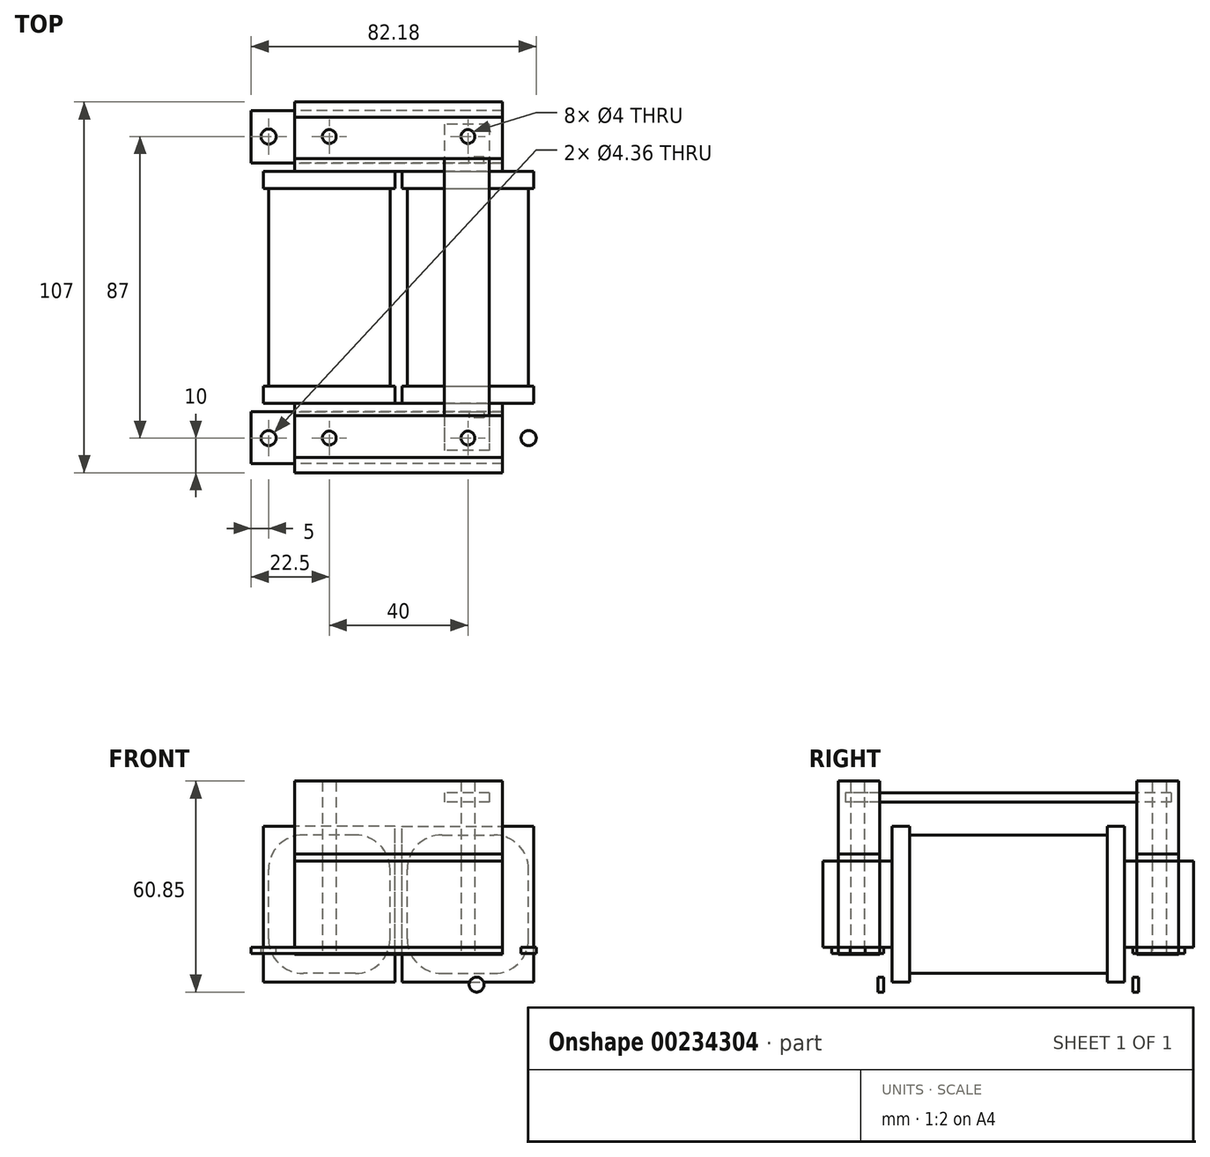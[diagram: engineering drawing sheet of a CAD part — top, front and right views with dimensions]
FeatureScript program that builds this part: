
annotation { "Feature Type Name" : "Feature", "Feature Type Description" : "" }
export const myFeature = defineFeature(function(context is Context, id is Id, definition is map)
    precondition{}
    {
        {
            var Q0;
            Q0=qCreatedBy(makeId("Front.planeOp"),FACE);
            var sketch = newSketch(context, id + "F0", { "sketchPlane" : qUnion([Q0])});
            skLineSegment(sketch, "E0.bottom", {"start": v(30, -12.5) * mm, "end": v(-30, -12.5) * mm});
            skLineSegment(sketch, "E0.top", {"start": v(30, 12.5) * mm, "end": v(-30, 12.5) * mm});
            skLineSegment(sketch, "E0.left", {"start": v(30, -12.5) * mm, "end": v(30, 12.5) * mm});
            skLineSegment(sketch, "E0.right", {"start": v(-30, -12.5) * mm, "end": v(-30, 12.5) * mm});
            skPoint(sketch, "E0.middle", {"position": v(0, 0) * mm});
            skLineSegment(sketch, "E1", {"start": v(-10, -12.5) * mm, "end": v(-10, 12.5) * mm});
            skLineSegment(sketch, "E2.MirrorCS", {"start": v(10, -12.5) * mm, "end": v(10, 12.5) * mm});
            skPoint(sketch, "E3", {"position": v(-20, 0) * mm});
            skLineSegment(sketch, "E4.bottom", {"start": v(-1, -22.5) * mm, "end": v(-39, -22.5) * mm});
            skLineSegment(sketch, "E4.top", {"start": v(-1, 22.5) * mm, "end": v(-39, 22.5) * mm});
            skLineSegment(sketch, "E4.left", {"start": v(-1, -22.5) * mm, "end": v(-1, 22.5) * mm});
            skLineSegment(sketch, "E4.right", {"start": v(-39, -22.5) * mm, "end": v(-39, 22.5) * mm});
            skLineSegment(sketch, "E5.bottom", {"start": v(-12.5, -20) * mm, "end": v(-27.5, -20) * mm});
            skLineSegment(sketch, "E5.top", {"start": v(-12.5, 20) * mm, "end": v(-27.5, 20) * mm});
            skLineSegment(sketch, "E5.left", {"start": v(-2.5, -10) * mm, "end": v(-2.5, 10) * mm});
            skLineSegment(sketch, "E5.right", {"start": v(-37.5, -10) * mm, "end": v(-37.5, 10) * mm});
            skPoint(sketch, "E6.visualSharp", {"position": v(-37.5, 20) * mm});
            skArc(sketch, "E6.filletArc", {"start": v(-27.5, 20) * mm, "mid": v(-34.57, 17.07) * mm, "end": v(-37.5, 10) * mm});
            skPoint(sketch, "E7.visualSharp", {"position": v(-2.5, 20) * mm});
            skArc(sketch, "E7.filletArc", {"start": v(-2.5, 10) * mm, "mid": v(-5.43, 17.07) * mm, "end": v(-12.5, 20) * mm});
            skPoint(sketch, "E8.visualSharp", {"position": v(-2.5, -20) * mm});
            skArc(sketch, "E8.filletArc", {"start": v(-12.5, -20) * mm, "mid": v(-5.43, -17.07) * mm, "end": v(-2.5, -10) * mm});
            skPoint(sketch, "E9.visualSharp", {"position": v(-37.5, -20) * mm});
            skArc(sketch, "E9.filletArc", {"start": v(-37.5, -10) * mm, "mid": v(-34.57, -17.07) * mm, "end": v(-27.5, -20) * mm});
            skLineSegment(sketch, "E10.MirrorCS", {"start": v(1, -22.5) * mm, "end": v(1, 22.5) * mm});
            skLineSegment(sketch, "E11.MirrorCS", {"start": v(1, 22.5) * mm, "end": v(39, 22.5) * mm});
            skLineSegment(sketch, "E12.MirrorCS", {"start": v(39, -22.5) * mm, "end": v(39, 22.5) * mm});
            skLineSegment(sketch, "E13.MirrorCS", {"start": v(1, -22.5) * mm, "end": v(39, -22.5) * mm});
            skLineSegment(sketch, "E14.MirrorCS", {"start": v(12.5, 20) * mm, "end": v(27.5, 20) * mm});
            skArc(sketch, "E15.MirrorCS", {"start": v(2.5, 10) * mm, "mid": v(5.43, 17.07) * mm, "end": v(12.5, 20) * mm});
            skLineSegment(sketch, "E16.MirrorCS", {"start": v(2.5, -10) * mm, "end": v(2.5, 10) * mm});
            skArc(sketch, "E17.MirrorCS", {"start": v(12.5, -20) * mm, "mid": v(5.43, -17.07) * mm, "end": v(2.5, -10) * mm});
            skLineSegment(sketch, "E18.MirrorCS", {"start": v(12.5, -20) * mm, "end": v(27.5, -20) * mm});
            skArc(sketch, "E19.MirrorCS", {"start": v(37.5, -10) * mm, "mid": v(34.57, -17.07) * mm, "end": v(27.5, -20) * mm});
            skLineSegment(sketch, "E20.MirrorCS", {"start": v(37.5, -10) * mm, "end": v(37.5, 10) * mm});
            skArc(sketch, "E21.MirrorCS", {"start": v(27.5, 20) * mm, "mid": v(34.57, 17.07) * mm, "end": v(37.5, 10) * mm});
            skSolve(sketch);
        }
        {
            var Q0;
            {var subQ0=sQuery(id+"F0.wireOp",EDGE,"E0.right");Q0=makeQuery(id+"F0.imprint","IMPRINT",FACE,{"disambiguationData":[TD([[makeQuery(id+"F0.imprint","IMPRINT",EDGE,{"derivedFrom":subQ0}),-1.0]])]});}
            var Q1;
            {var subQ0=sQuery(id+"F0.wireOp",EDGE,"E0.left");Q1=makeQuery(id+"F0.imprint","IMPRINT",FACE,{"disambiguationData":[TD([[makeQuery(id+"F0.imprint","IMPRINT",EDGE,{"derivedFrom":subQ0}),1.0]])]});}
            var Q2;
            {var subQ4=sQuery(id+"F0.wireOp",EDGE,"E0.right");Q2=makeQuery(id+"F0.imprint","IMPRINT",FACE,{"disambiguationData":[TD([[makeQuery(id+"F0.imprint","IMPRINT",EDGE,{"derivedFrom":subQ4}),1.0]])]});}
            var Q3;
            {var subQ1=sQuery(id+"F0.wireOp",EDGE,"E1");Q3=makeQuery(id+"F0.imprint","IMPRINT",FACE,{"disambiguationData":[TD([[makeQuery(id+"F0.imprint","IMPRINT",EDGE,{"derivedFrom":subQ1}),-1.0]])]});}
            var Q4;
            {var subQ0=sQuery(id+"F0.wireOp",EDGE,"E2.MirrorCS");Q4=makeQuery(id+"F0.imprint","IMPRINT",FACE,{"disambiguationData":[TD([[makeQuery(id+"F0.imprint","IMPRINT",EDGE,{"derivedFrom":subQ0}),1.0]])]});}
            var Q5;
            {var subQ1=sQuery(id+"F0.wireOp",EDGE,"E0.left");Q5=makeQuery(id+"F0.imprint","IMPRINT",FACE,{"disambiguationData":[TD([[makeQuery(id+"F0.imprint","IMPRINT",EDGE,{"derivedFrom":subQ1}),-1.0]])]});}
            extrude(context, id + "F1", {"entities" : qUnion([Q0, Q1, Q2, Q3, Q4, Q5]), "depth" : 57 * mm, "symmetric" : true});
        }
        {
            var Q0;
            Q0=makeQuery(id+"F1.opExtrude","CAP_FACE",FACE,{"disambiguationData":[OSD([sQuery(id+"F0.wireOp",EDGE,"E5.bottom"),sQuery(id+"F0.wireOp",EDGE,"E5.top"),sQuery(id+"F0.wireOp",EDGE,"E5.left"),sQuery(id+"F0.wireOp",EDGE,"E5.right"),sQuery(id+"F0.wireOp",EDGE,"E6.filletArc"),sQuery(id+"F0.wireOp",EDGE,"E7.filletArc"),sQuery(id+"F0.wireOp",EDGE,"E8.filletArc"),sQuery(id+"F0.wireOp",EDGE,"E9.filletArc")])],"isStart":false});
            var sketch = newSketch(context, id + "F2", { "sketchPlane" : qUnion([Q0])});
            skLineSegment(sketch, "E22.bottom", {"start": v(-1, -22.5) * mm, "end": v(-39, -22.5) * mm});
            skLineSegment(sketch, "E22.top", {"start": v(-1, 22.5) * mm, "end": v(-39, 22.5) * mm});
            skLineSegment(sketch, "E22.left", {"start": v(-1, -22.5) * mm, "end": v(-1, 22.5) * mm});
            skLineSegment(sketch, "E22.right", {"start": v(-39, -22.5) * mm, "end": v(-39, 22.5) * mm});
            skPoint(sketch, "E22.middle", {"position": v(-20, 0) * mm});
            skPoint(sketch, "E22.middle.positionSnap0", {"position": v(-20, 20) * mm});
            skPoint(sketch, "E22.centerSnap0", {"position": v(-20, 20) * mm});
            skSolve(sketch);
        }
        {
            var Q0;
            Q0=makeQuery(id+"F2.imprint","IMPRINT",FACE,{"disambiguationData":[TD([[makeQuery(id+"F2.imprint","IMPRINT",EDGE,{"derivedFrom":sQuery(id+"F2.wireOp",EDGE,"E22.bottom")}),-1.0]])]});
            var Q1;
            Q1=makeQuery(id+"F2.imprint","IMPRINT",FACE,{"disambiguationData":[TD([[makeQuery(id+"F2.imprint","IMPRINT",EDGE,{"derivedFrom":makeQuery(id+"F1.opExtrude","CAP_EDGE",EDGE,{"disambiguationData":[OSD([sQuery(id+"F0.wireOp",EDGE,"E5.bottom")])],"isStart":false})}),-1.0]])]});
            extrude(context, id + "F3", {"entities" : qUnion([Q0, Q1]), "depth" : 5 * mm});
        }
        {
            var Q0;
            Q0=makeQuery(id+"F3.opExtrude","SWEPT_BODY",BODY,{"disambiguationData":[OSD([sQuery(id+"F0.wireOp",EDGE,"E5.bottom"),sQuery(id+"F0.wireOp",EDGE,"E5.top"),sQuery(id+"F0.wireOp",EDGE,"E5.left"),sQuery(id+"F0.wireOp",EDGE,"E5.right"),sQuery(id+"F0.wireOp",EDGE,"E6.filletArc"),sQuery(id+"F0.wireOp",EDGE,"E7.filletArc"),sQuery(id+"F0.wireOp",EDGE,"E8.filletArc"),sQuery(id+"F0.wireOp",EDGE,"E9.filletArc"),sQuery(id+"F2.wireOp",EDGE,"E22.bottom"),sQuery(id+"F2.wireOp",EDGE,"E22.top"),sQuery(id+"F2.wireOp",EDGE,"E22.left"),sQuery(id+"F2.wireOp",EDGE,"E22.right")])]});
            var Q1;
            Q1=qCreatedBy(makeId("Right.planeOp"),FACE);
            mirror(context, id + "F4", {"entities" : qUnion([Q0]), "mirrorPlane" : qUnion([Q1])});
        }
        {
            var Q0;
            Q0=makeQuery(id+"F3.opExtrude","SWEPT_BODY",BODY,{"disambiguationData":[OSD([sQuery(id+"F0.wireOp",EDGE,"E5.bottom"),sQuery(id+"F0.wireOp",EDGE,"E5.top"),sQuery(id+"F0.wireOp",EDGE,"E5.left"),sQuery(id+"F0.wireOp",EDGE,"E5.right"),sQuery(id+"F0.wireOp",EDGE,"E6.filletArc"),sQuery(id+"F0.wireOp",EDGE,"E7.filletArc"),sQuery(id+"F0.wireOp",EDGE,"E8.filletArc"),sQuery(id+"F0.wireOp",EDGE,"E9.filletArc"),sQuery(id+"F2.wireOp",EDGE,"E22.bottom"),sQuery(id+"F2.wireOp",EDGE,"E22.top"),sQuery(id+"F2.wireOp",EDGE,"E22.left"),sQuery(id+"F2.wireOp",EDGE,"E22.right")])]});
            var Q1;
            Q1=makeQuery(id+"F4.opPattern","COPY",BODY,{"derivedFrom":makeQuery(id+"F3.opExtrude","SWEPT_BODY",BODY,{"disambiguationData":[OSD([sQuery(id+"F0.wireOp",EDGE,"E5.bottom"),sQuery(id+"F0.wireOp",EDGE,"E5.top"),sQuery(id+"F0.wireOp",EDGE,"E5.left"),sQuery(id+"F0.wireOp",EDGE,"E5.right"),sQuery(id+"F0.wireOp",EDGE,"E6.filletArc"),sQuery(id+"F0.wireOp",EDGE,"E7.filletArc"),sQuery(id+"F0.wireOp",EDGE,"E8.filletArc"),sQuery(id+"F0.wireOp",EDGE,"E9.filletArc"),sQuery(id+"F2.wireOp",EDGE,"E22.bottom"),sQuery(id+"F2.wireOp",EDGE,"E22.top"),sQuery(id+"F2.wireOp",EDGE,"E22.left"),sQuery(id+"F2.wireOp",EDGE,"E22.right")])]}),"instanceName":"1"});
            var Q2;
            Q2=qCreatedBy(makeId("Front.planeOp"),FACE);
            mirror(context, id + "F5", {"entities" : qUnion([Q0, Q1]), "mirrorPlane" : qUnion([Q2])});
        }
        {
            var Q0;
            Q0=makeQuery(id+"F3.opExtrude","CAP_FACE",FACE,{"disambiguationData":[OSD([sQuery(id+"F2.wireOp",EDGE,"E22.bottom"),sQuery(id+"F2.wireOp",EDGE,"E22.top"),sQuery(id+"F2.wireOp",EDGE,"E22.left"),sQuery(id+"F2.wireOp",EDGE,"E22.right")])],"isStart":false});
            var sketch = newSketch(context, id + "F6", { "sketchPlane" : qUnion([Q0])});
            skLineSegment(sketch, "E23.bottom", {"start": v(30, -12.5) * mm, "end": v(-30, -12.5) * mm});
            skLineSegment(sketch, "E23.top", {"start": v(30, 12.5) * mm, "end": v(-30, 12.5) * mm});
            skLineSegment(sketch, "E23.left", {"start": v(30, -12.5) * mm, "end": v(30, 12.5) * mm});
            skLineSegment(sketch, "E23.right", {"start": v(-30, -12.5) * mm, "end": v(-30, 12.5) * mm});
            skPoint(sketch, "E23.middle", {"position": v(0, 0) * mm});
            skSolve(sketch);
        }
        {
            var Q0;
            {var subQ0=sQuery(id+"F6.wireOp",EDGE,"E23.right");Q0=makeQuery(id+"F6.imprint","IMPRINT",FACE,{"disambiguationData":[TD([[makeQuery(id+"F6.imprint","IMPRINT",EDGE,{"derivedFrom":subQ0}),-1.0]])]});}
            var Q1;
            {var subQ0=sQuery(id+"F6.wireOp",EDGE,"E23.left");Q1=makeQuery(id+"F6.imprint","IMPRINT",FACE,{"disambiguationData":[TD([[makeQuery(id+"F6.imprint","IMPRINT",EDGE,{"derivedFrom":subQ0}),1.0]])]});}
            extrude(context, id + "F7", {"entities" : qUnion([Q0, Q1]), "depth" : 20 * mm});
        }
        {
            var Q0;
            Q0=makeQuery(id+"F7.opExtrude","SWEPT_BODY",BODY,{"disambiguationData":[OSD([sQuery(id+"F6.wireOp",EDGE,"E23.bottom"),sQuery(id+"F6.wireOp",EDGE,"E23.top"),sQuery(id+"F6.wireOp",EDGE,"E23.left"),sQuery(id+"F6.wireOp",EDGE,"E23.right")])]});
            var Q1;
            Q1=qCreatedBy(makeId("Front.planeOp"),FACE);
            mirror(context, id + "F8", {"entities" : qUnion([Q0]), "mirrorPlane" : qUnion([Q1])});
        }
        {
            var Q0;
            Q0=makeQuery(id+"F7.opExtrude","SWEPT_FACE",FACE,{"disambiguationData":[OSD([sQuery(id+"F6.wireOp",EDGE,"E23.top")])]});
            var sketch = newSketch(context, id + "F9", { "sketchPlane" : qUnion([Q0])});
            skLineSegment(sketch, "E24.bottom", {"start": v(30, -49.08) * mm, "end": v(-30, -49.08) * mm});
            skLineSegment(sketch, "E24.top", {"start": v(30, -37.08) * mm, "end": v(-30, -37.08) * mm});
            skLineSegment(sketch, "E24.left", {"start": v(30, -49.08) * mm, "end": v(30, -37.08) * mm});
            skLineSegment(sketch, "E24.right", {"start": v(-30, -49.08) * mm, "end": v(-30, -37.08) * mm});
            skPoint(sketch, "E24.middle", {"position": v(0, -43.08) * mm});
            skCircle(sketch, "E25", {"center": v(-20, -43.5) * mm, "radius": 2 * mm});
            skCircle(sketch, "E26.MirrorC", {"center": v(20, -43.5) * mm, "radius": 2 * mm});
            skSolve(sketch);
        }
        {
            var Q0;
            Q0=makeQuery(id+"F9.imprint","IMPRINT",FACE,{"disambiguationData":[TD([[makeQuery(id+"F9.imprint","IMPRINT",EDGE,{"derivedFrom":sQuery(id+"F9.wireOp",EDGE,"E24.bottom")}),-1.0]])]});
            extrude(context, id + "F10", {"entities" : qUnion([Q0]), "depth" : 2 * mm});
        }
        {
            var Q0;
            Q0=makeQuery(id+"F10.opExtrude","SWEPT_BODY",BODY,{"disambiguationData":[OSD([sQuery(id+"F9.wireOp",EDGE,"E24.bottom"),sQuery(id+"F9.wireOp",EDGE,"E24.top"),sQuery(id+"F9.wireOp",EDGE,"E24.left"),sQuery(id+"F9.wireOp",EDGE,"E24.right"),sQuery(id+"F9.wireOp",EDGE,"E25"),sQuery(id+"F9.wireOp",EDGE,"E26.MirrorC")])]});
            var Q1;
            Q1=makeQuery(id+"FH1xh7xZK8g8Pgw_5.opPattern","COPY",BODY,{"derivedFrom":makeQuery(id+"F10.opExtrude","SWEPT_BODY",BODY,{"disambiguationData":[OSD([sQuery(id+"F9.wireOp",EDGE,"E24.bottom"),sQuery(id+"F9.wireOp",EDGE,"E24.top"),sQuery(id+"F9.wireOp",EDGE,"E24.left"),sQuery(id+"F9.wireOp",EDGE,"E24.right"),sQuery(id+"F9.wireOp",EDGE,"E25"),sQuery(id+"F9.wireOp",EDGE,"E26.MirrorC")])]}),"instanceName":"1"});
            var Q2;
            Q2=qCreatedBy(makeId("Front.planeOp"),FACE);
            mirror(context, id + "F11", {"entities" : qUnion([Q0, Q1]), "mirrorPlane" : qUnion([Q2])});
        }
        {
            var Q0;
            Q0=makeQuery(id+"F7.opExtrude","SWEPT_FACE",FACE,{"disambiguationData":[OSD([sQuery(id+"F6.wireOp",EDGE,"E23.bottom")])]});
            var sketch = newSketch(context, id + "F12", { "sketchPlane" : qUnion([Q0])});
            skLineSegment(sketch, "E27.bottom", {"start": v(42.5, 35.92) * mm, "end": v(-42.5, 35.92) * mm});
            skLineSegment(sketch, "E27.top", {"start": v(42.5, 50.92) * mm, "end": v(-42.5, 50.92) * mm});
            skLineSegment(sketch, "E27.left", {"start": v(42.5, 35.92) * mm, "end": v(42.5, 50.92) * mm});
            skLineSegment(sketch, "E27.right", {"start": v(-42.5, 35.92) * mm, "end": v(-42.5, 50.92) * mm});
            skPoint(sketch, "E27.middle", {"position": v(0, 43.42) * mm});
            skCircle(sketch, "E28", {"center": v(-37.5, 43.5) * mm, "radius": 2.18 * mm});
            skPoint(sketch, "E28.centerSnap0", {"position": v(-30, 43.5) * mm});
            skCircle(sketch, "E29.MirrorC", {"center": v(37.5, 43.5) * mm, "radius": 2.18 * mm});
            skLineSegment(sketch, "E30", {"start": v(-42.5, 37.62) * mm, "end": v(42.5, 37.62) * mm});
            skSolve(sketch);
        }
        {
            var Q0;
            {var subQ5=sQuery(id+"F12.wireOp",EDGE,"E27.right");Q0=makeQuery(id+"F12.imprint","IMPRINT",FACE,{"disambiguationData":[TD([[makeQuery(id+"F12.imprint","IMPRINT",EDGE,{"derivedFrom":subQ5}),-1.0]])]});}
            var Q1;
            {var subQ0=sQuery(id+"F6.wireOp",EDGE,"E23.bottom");var subQ1=makeQuery(id+"F7.opExtrude","SWEPT_FACE",FACE,{"disambiguationData":[OSD([subQ0])]});Q1=makeQuery(id+"F12.imprint","IMPRINT",FACE,{"disambiguationData":[TD([[makeQuery(id+"F12.imprint","IMPRINT",EDGE,{"derivedFrom":makeQuery(id+"FQ7v0Hopz4n4mA3_5.boolean.opBoolean","INTERSECT",EDGE,{"derivedFrom":[subQ1,makeQuery(id+"FQ7v0Hopz4n4mA3_5.opExtrude","SWEPT_FACE",FACE,{"disambiguationData":[OSD([sQuery(id+"F9.wireOp",EDGE,"E25")])]})]})}),-1.0]])]});}
            var Q2;
            {var subQ0=sQuery(id+"F12.wireOp",EDGE,"E27.left");Q2=makeQuery(id+"F12.imprint","IMPRINT",FACE,{"disambiguationData":[TD([[makeQuery(id+"F12.imprint","IMPRINT",EDGE,{"derivedFrom":subQ0}),1.0]])]});}
            var Q3;
            Q3=makeQuery(id+"F12.imprint","IMPRINT",FACE,{"disambiguationData":[TD([[makeQuery(id+"F12.imprint","IMPRINT",EDGE,{"derivedFrom":sQuery(id+"F12.wireOp",EDGE,"E28")}),-1.0]])]});
            var Q4;
            {var subQ0=sQuery(id+"F12.wireOp",EDGE,"E27.bottom");var subQ1=sQuery(id+"F6.wireOp",EDGE,"E23.bottom");var subQ2=makeQuery(id+"F7.opExtrude","SWEPT_EDGE",EDGE,{"disambiguationData":[OSD([subQ1,sQuery(id+"F6.wireOp",EDGE,"E23.left")])]});var subQ3=makeQuery(id+"F12.imprint","INTERSECT",VERTEX,{"derivedFrom":[subQ2,subQ0]});Q4=makeQuery(id+"F12.imprint","IMPRINT",FACE,{"disambiguationData":[TD([[makeQuery(id+"F12.imprint","IMPRINT",EDGE,{"disambiguationData":[TD([[subQ3,-1.0]])],"derivedFrom":subQ0}),-1.0]])]});}
            var Q5;
            Q5=makeQuery(id+"F12.imprint","IMPRINT",FACE,{"disambiguationData":[TD([[makeQuery(id+"F12.imprint","IMPRINT",EDGE,{"derivedFrom":sQuery(id+"F12.wireOp",EDGE,"E29.MirrorC")}),1.0]])]});
            var Q6;
            {var subQ0=sQuery(id+"F12.wireOp",EDGE,"E27.top");var subQ1=sQuery(id+"F6.wireOp",EDGE,"E23.bottom");var subQ2=makeQuery(id+"F7.opExtrude","SWEPT_EDGE",EDGE,{"disambiguationData":[OSD([subQ1,sQuery(id+"F6.wireOp",EDGE,"E23.left")])]});var subQ3=makeQuery(id+"F12.imprint","INTERSECT",VERTEX,{"derivedFrom":[subQ2,subQ0]});Q6=makeQuery(id+"F12.imprint","IMPRINT",FACE,{"disambiguationData":[TD([[makeQuery(id+"F12.imprint","IMPRINT",EDGE,{"disambiguationData":[TD([[subQ3,-1.0]])],"derivedFrom":subQ0}),1.0]])]});}
            extrude(context, id + "F13", {"entities" : qUnion([Q0, Q1, Q2, Q3, Q4, Q5, Q6]), "depth" : 1.7 * mm});
        }
        {
            var Q0;
            Q0=makeQuery(id+"F13.opExtrude","CAP_FACE",FACE,{"disambiguationData":[OSD([sQuery(id+"F6.wireOp",EDGE,"E23.bottom"),sQuery(id+"F9.wireOp",EDGE,"E25"),sQuery(id+"F9.wireOp",EDGE,"E26.MirrorC"),sQuery(id+"F12.wireOp",EDGE,"E27.bottom"),sQuery(id+"F12.wireOp",EDGE,"E27.top"),sQuery(id+"F12.wireOp",EDGE,"E27.left"),sQuery(id+"F12.wireOp",EDGE,"E27.right"),sQuery(id+"F12.wireOp",EDGE,"E28"),sQuery(id+"F12.wireOp",EDGE,"E29.MirrorC")])],"isStart":false});
            var sketch = newSketch(context, id + "F14", { "sketchPlane" : qUnion([Q0])});
            skLineSegment(sketch, "E31.bottom", {"start": v(-42.5, 35.92) * mm, "end": v(42.5, 35.92) * mm});
            skLineSegment(sketch, "E31.top", {"start": v(-42.5, 37.62) * mm, "end": v(42.5, 37.62) * mm});
            skLineSegment(sketch, "E31.left", {"start": v(-42.5, 35.92) * mm, "end": v(-42.5, 37.62) * mm});
            skLineSegment(sketch, "E31.right", {"start": v(42.5, 35.92) * mm, "end": v(42.5, 37.62) * mm});
            skSolve(sketch);
        }
        {
            var Q0;
            Q0=makeQuery(id+"F14.imprint","IMPRINT",FACE,{"disambiguationData":[TD([[makeQuery(id+"F14.imprint","IMPRINT",EDGE,{"derivedFrom":sQuery(id+"F14.wireOp",EDGE,"E31.bottom")}),-1.0]])]});
            extrude(context, id + "F15", {"entities" : qUnion([Q0]), "operationType" : NewBodyOperationType.ADD, "depth" : 14 * mm});
        }
        {
            var Q0;
            Q0=makeQuery(id+"F15.opExtrude","SWEPT_FACE",FACE,{"disambiguationData":[OSD([sQuery(id+"F14.wireOp",EDGE,"E31.top")])]});
            var sketch = newSketch(context, id + "F16", { "sketchPlane" : qUnion([Q0])});
            skCircle(sketch, "E32", {"center": v(-22.5, -23.2) * mm, "radius": 2.15 * mm});
            skCircle(sketch, "E33.MirrorC", {"center": v(22.5, -23.2) * mm, "radius": 2.15 * mm});
            skSolve(sketch);
        }
        {
            var Q0;
            Q0=makeQuery(id+"F16.imprint","IMPRINT",FACE,{"disambiguationData":[TD([[makeQuery(id+"F16.imprint","IMPRINT",EDGE,{"derivedFrom":sQuery(id+"F16.wireOp",EDGE,"E32")}),1.0]])]});
            var Q1;
            Q1=makeQuery(id+"F16.imprint","IMPRINT",FACE,{"disambiguationData":[TD([[makeQuery(id+"F16.imprint","IMPRINT",EDGE,{"derivedFrom":sQuery(id+"F16.wireOp",EDGE,"E33.MirrorC")}),-1.0]])]});
            extrude(context, id + "F17", {"entities" : qUnion([Q0, Q1]), "operationType" : NewBodyOperationType.REMOVE, "endBound" : BoundingType.UP_TO_NEXT, "oppositeDirection" : true, "depth" : 25 * mm});
        }
        {
            var Q0;
            Q0=makeQuery(id+"F13.opExtrude","SWEPT_BODY",BODY,{"disambiguationData":[OSD([sQuery(id+"F6.wireOp",EDGE,"E23.bottom"),sQuery(id+"F9.wireOp",EDGE,"E25"),sQuery(id+"F9.wireOp",EDGE,"E26.MirrorC"),sQuery(id+"F12.wireOp",EDGE,"E27.bottom"),sQuery(id+"F12.wireOp",EDGE,"E27.top"),sQuery(id+"F12.wireOp",EDGE,"E27.left"),sQuery(id+"F12.wireOp",EDGE,"E27.right"),sQuery(id+"F12.wireOp",EDGE,"E28"),sQuery(id+"F12.wireOp",EDGE,"E29.MirrorC")])]});
            var Q1;
            Q1=qCreatedBy(makeId("Front.planeOp"),FACE);
            mirror(context, id + "F18", {"entities" : qUnion([Q0]), "mirrorPlane" : qUnion([Q1])});
        }
        {
            var Q0;
            Q0=makeQuery(id+"F10.opExtrude","CAP_FACE",FACE,{"disambiguationData":[OSD([sQuery(id+"F9.wireOp",EDGE,"E24.bottom"),sQuery(id+"F9.wireOp",EDGE,"E24.top"),sQuery(id+"F9.wireOp",EDGE,"E24.left"),sQuery(id+"F9.wireOp",EDGE,"E24.right"),sQuery(id+"F9.wireOp",EDGE,"E25"),sQuery(id+"F9.wireOp",EDGE,"E26.MirrorC")])],"isStart":false});
            cPlane(context, id + "F19", {"entities" : qUnion([Q0]), "cplaneType" : CPlaneType.OFFSET, "offset" : 15 * mm, "width" : 150 * mm, "height" : 150 * mm});
        }
        {
            var Q0;
            Q0=qCreatedBy(id+"F19.planeOp",FACE);
            var sketch = newSketch(context, id + "F20", { "sketchPlane" : qUnion([Q0])});
            skLineSegment(sketch, "E34.bottom", {"start": v(26.17, 47) * mm, "end": v(13.17, 47) * mm});
            skLineSegment(sketch, "E34.top", {"start": v(26.17, -47) * mm, "end": v(13.17, -47) * mm});
            skLineSegment(sketch, "E34.left", {"start": v(26.17, 47) * mm, "end": v(26.17, -47) * mm});
            skLineSegment(sketch, "E34.right", {"start": v(13.17, 47) * mm, "end": v(13.17, -47) * mm});
            skPoint(sketch, "E34.middle", {"position": v(19.67, 0) * mm});
            skSolve(sketch);
        }
        {
            var Q0;
            Q0=makeQuery(id+"F20.imprint","IMPRINT",FACE,{"disambiguationData":[TD([[makeQuery(id+"F20.imprint","IMPRINT",EDGE,{"derivedFrom":sQuery(id+"F20.wireOp",EDGE,"E34.bottom")}),1.0]])]});
            extrude(context, id + "F21", {"entities" : qUnion([Q0]), "depth" : 2.6 * mm});
        }
        {
            var Q0;
            Q0=makeQuery(id+"F9.imprint","IMPRINT",FACE,{"disambiguationData":[TD([[makeQuery(id+"F9.imprint","IMPRINT",EDGE,{"derivedFrom":sQuery(id+"F9.wireOp",EDGE,"E26.MirrorC")}),-1.0]])]});
            extrude(context, id + "F22", {"entities" : qUnion([Q0]), "depth" : 23 * mm, "hasSecondDirection" : true, "secondDirectionOppositeDirection" : true, "secondDirectionDepth" : 27 * mm});
        }
        {
            var Q0;
            Q0=makeQuery(id+"F22.opExtrude","SWEPT_BODY",BODY,{"disambiguationData":[OSD([sQuery(id+"F9.wireOp",EDGE,"E26.MirrorC")])]});
            var Q1;
            Q1=qCreatedBy(makeId("Front.planeOp"),FACE);
            mirror(context, id + "F23", {"entities" : qUnion([Q0]), "mirrorPlane" : qUnion([Q1])});
        }
    });
